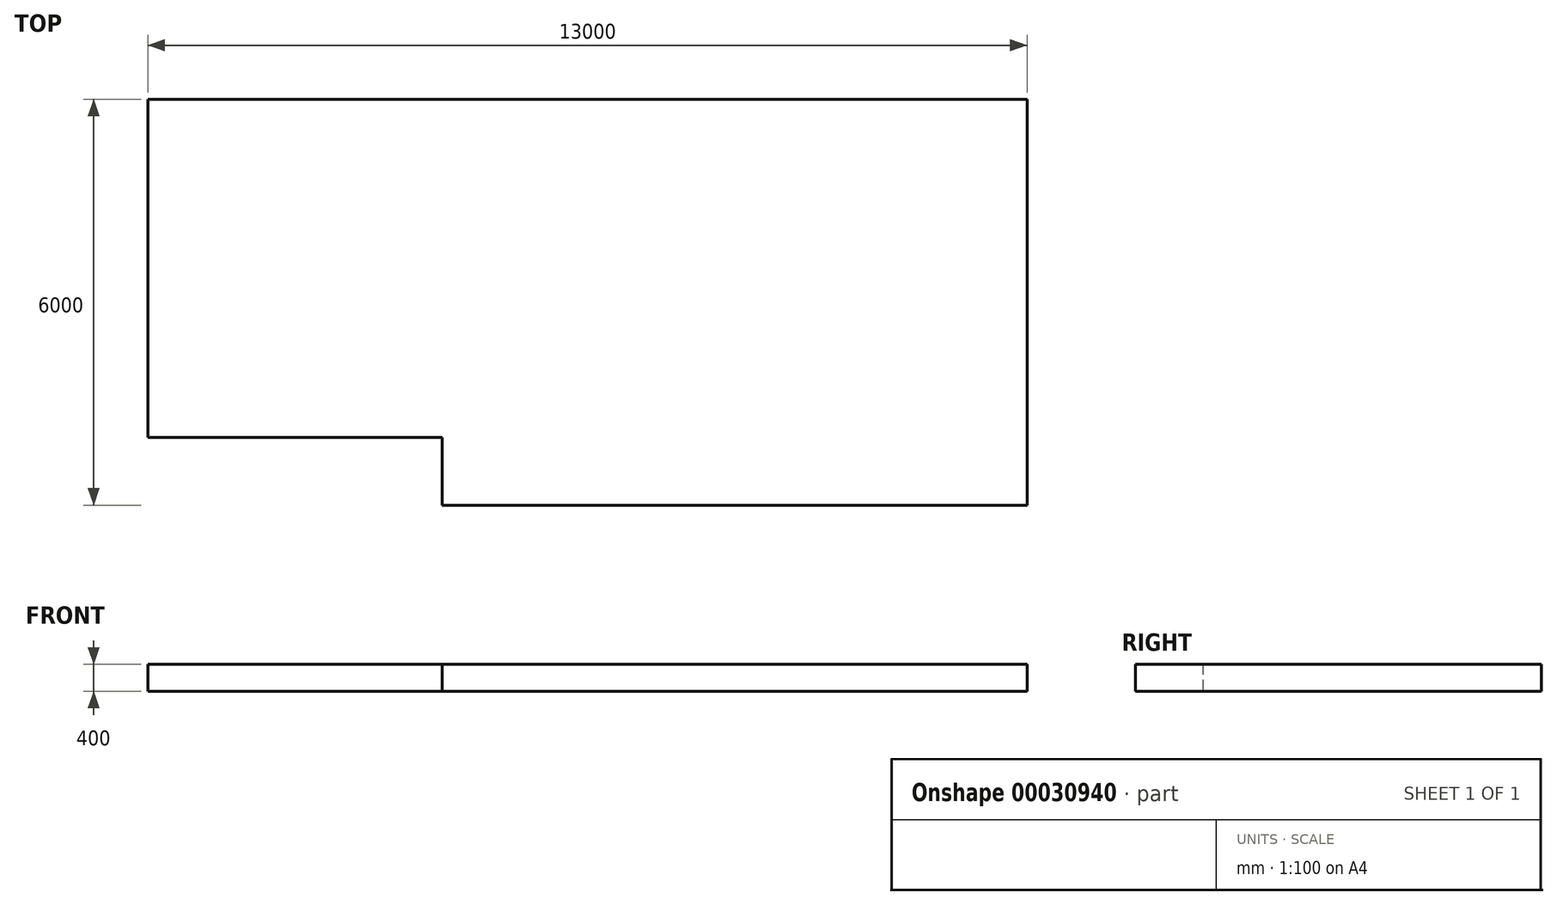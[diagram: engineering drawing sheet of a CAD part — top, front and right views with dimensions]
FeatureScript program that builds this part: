
annotation { "Feature Type Name" : "Feature", "Feature Type Description" : "" }
export const myFeature = defineFeature(function(context is Context, id is Id, definition is map)
    precondition{}
    {
        {
            var Q0;
            Q0=qCreatedBy(makeId("Top.planeOp"),FACE);
            var sketch = newSketch(context, id + "F0", { "sketchPlane" : qUnion([Q0])});
            skLineSegment(sketch, "E0", {"start": v(0, 0) * mm, "end": v(4350, 0) * mm});
            skLineSegment(sketch, "E1", {"start": v(4350, -1000) * mm, "end": v(4350, 0) * mm});
            skLineSegment(sketch, "E2", {"start": v(4350, -1000) * mm, "end": v(13000, -1000) * mm});
            skLineSegment(sketch, "E3", {"start": v(13000, -1000) * mm, "end": v(13000, 5000) * mm});
            skLineSegment(sketch, "E4", {"start": v(13000, 5000) * mm, "end": v(0, 5000) * mm});
            skLineSegment(sketch, "E5", {"start": v(0, 5000) * mm, "end": v(0, 0) * mm});
            skSolve(sketch);
        }
        {
            var Q0;
            Q0 = qSketchRegion(id + "F0", true);
            extrude(context, id + "F1", {"entities" : qUnion([Q0]), "depth" : 400 * mm});
        }
    });
